FCSTD DOCUMENT  (FreeCAD 1.0R38806 (Git))
Label: modelo alambrico
License: All rights reserved
LicenseURL: https://en.wikipedia.org/wiki/All_rights_reserved
objects: Sketcher::SketchObject×1
note: 2 computed .brp shape members not serialized (recipe doc carries the construction recipe); baked Part::Feature solids carry a one-line shape summary decoded from their .brp

FEATURE [Sketcher::SketchObject] Sketch
  ArcFitTolerance = 1e-06
  FullyConstrained = false
  MakeInternals = false
  sketch-geometry (12):
    g0: LineSegment StartX=0 StartY=0 StartZ=0 EndX=-20.0041 EndY=20.0041 EndZ=0
    g1: LineSegment StartX=0 StartY=0 StartZ=0 EndX=5.22087 EndY=56.203 EndZ=0
    g2: LineSegment StartX=-20.0041 StartY=20.0041 StartZ=0 EndX=-14.7832 EndY=76.2071 EndZ=0
    g3: LineSegment StartX=-14.7832 StartY=76.2071 StartZ=0 EndX=5.22087 EndY=56.203 EndZ=0
    g4: LineSegment StartX=0 StartY=0 StartZ=0 EndX=-17.6777 EndY=17.6777 EndZ=0
    g5: LineSegment StartX=-17.6777 StartY=17.6777 StartZ=0 EndX=-13.5733 EndY=61.8616 EndZ=0
    g6: LineSegment StartX=-14.7832 StartY=76.2071 StartZ=0 EndX=33.5051 EndY=84.4873 EndZ=0
    g7: LineSegment StartX=5.22087 StartY=56.203 StartZ=0 EndX=33.5051 EndY=84.4873 EndZ=0
    g8: LineSegment StartX=33.5051 StartY=84.4873 StartZ=0 EndX=119.684 EndY=58.5403 EndZ=0
    g9: LineSegment StartX=119.684 StartY=58.5403 StartZ=0 EndX=91.3995 EndY=30.2561 EndZ=0
    g10: LineSegment StartX=-13.5733 StartY=61.8616 StartZ=0 EndX=91.3995 EndY=30.2561 EndZ=0
    g11: LineSegment StartX=91.3995 StartY=30.2561 StartZ=0 EndX=131.399 EndY=30.2561 EndZ=0
  constraints (31):
    c: Coincident(g0,g-1)
    c: Distance(g0,g0) = 28.29
    c: Angle(g0,g-1) = 0.785398
    c: Coincident(g1,g0)
    c: Coincident(g2,g0)
    c: Equal(g2,g1)
    c: Distance(g2,g2) = 56.445
    c: Coincident(g3,g2)
    c: Coincident(g3,g1)
    c: Parallel(g3,g0)
    c: Distance(g4) = 25
    c: Coincident(g4,g0)
    c: PointOnObject(g4,g0)
    c: Coincident(g5,g4)
    c: Parallel(g2,g5)
    c: Coincident(g6,g2)
    c: Coincident(g7,g1)
    c: Coincident(g7,g6)
    c: Angle(g7,g3) = 1.5708
    c: Distance(g7,g7) = 40
    c: Distance(g8) = 90
    c: Coincident(g8,g6)
    c: Coincident(g9,g8)
    c: Distance(g9,g9) = 40
    c: Parallel(g9,g7)
    c: Coincident(g10,g5)
    c: Coincident(g10,g9)
    c: PointOnObject(g1,g10)
    c: Distance(g11) = 40
    c: Coincident(g11,g9)
    c: Horizontal(g11)
